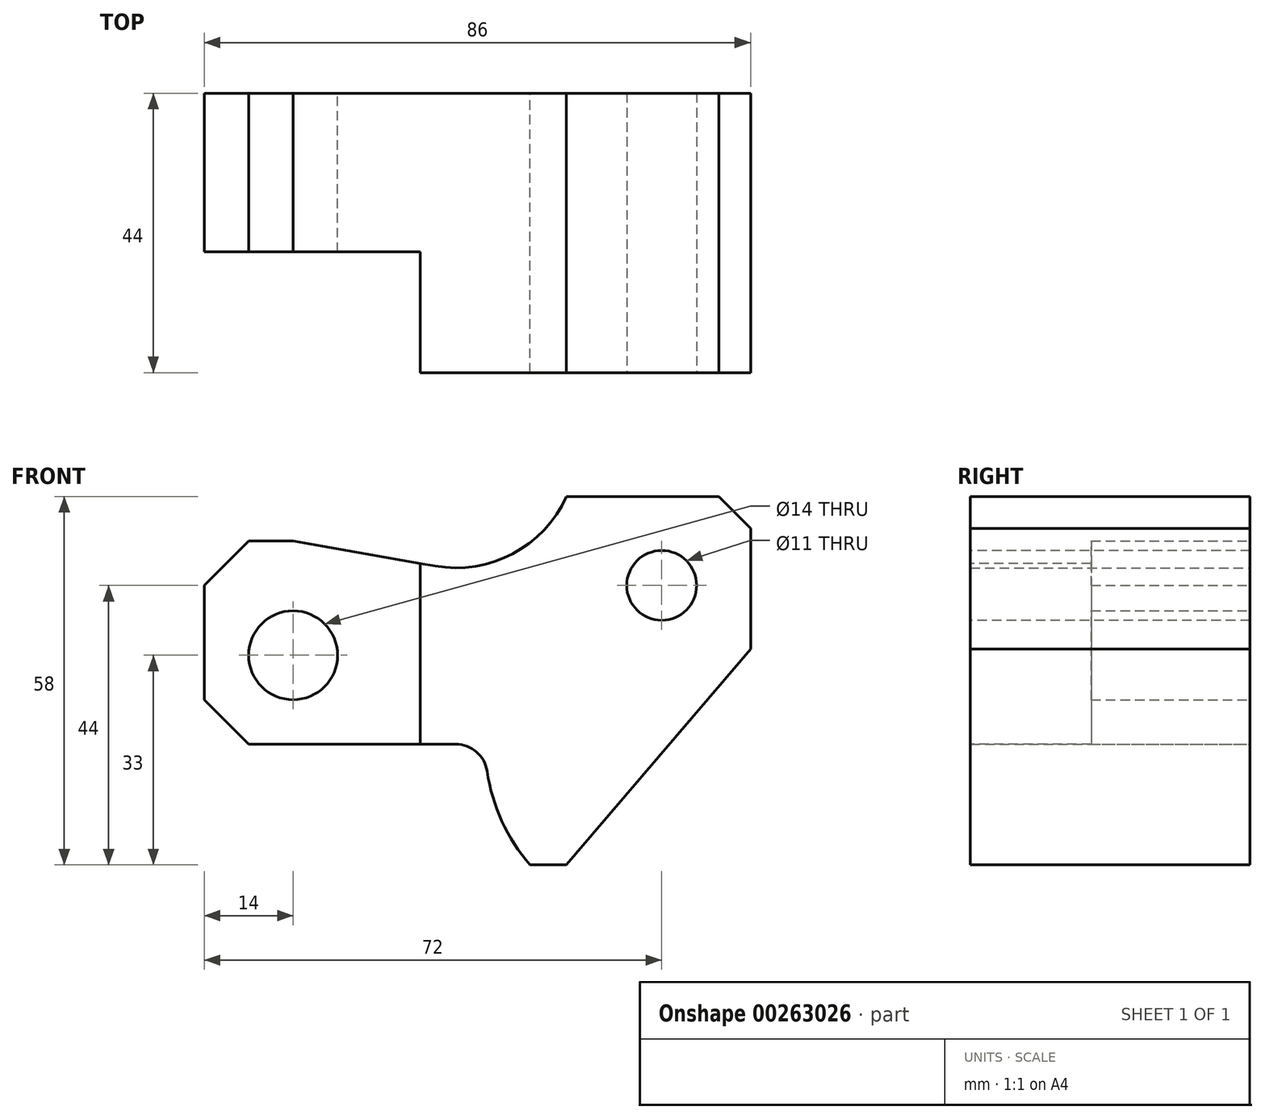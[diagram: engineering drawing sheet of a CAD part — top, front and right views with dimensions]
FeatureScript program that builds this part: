
annotation { "Feature Type Name" : "Feature", "Feature Type Description" : "" }
export const myFeature = defineFeature(function(context is Context, id is Id, definition is map)
    precondition{}
    {
        {
            var Q0;
            Q0=qCreatedBy(makeId("Front.planeOp"),FACE);
            var sketch = newSketch(context, id + "F0", { "sketchPlane" : qUnion([Q0])});
            skCircle(sketch, "E0", {"center": v(0, 0) * mm, "radius": 7 * mm});
            skLineSegment(sketch, "E1", {"start": v(-14, 11) * mm, "end": v(-14, -7) * mm});
            skLineSegment(sketch, "E2", {"start": v(-14, -7) * mm, "end": v(-7, -14) * mm});
            skLineSegment(sketch, "E3", {"start": v(-7, -14) * mm, "end": v(25.58, -14) * mm});
            skLineSegment(sketch, "E4", {"start": v(-14, 11) * mm, "end": v(-7, 18) * mm});
            skLineSegment(sketch, "E5", {"start": v(-7, 18) * mm, "end": v(0, 18) * mm});
            skLineSegment(sketch, "E6", {"start": v(0, 18) * mm, "end": v(22.36, 14.06) * mm});
            skArc(sketch, "E7", {"start": v(22.36, 14.06) * mm, "mid": v(34.56, 15.98) * mm, "end": v(43, 25) * mm});
            skArc(sketch, "E8", {"start": v(30.52, -18.26) * mm, "mid": v(28.84, -15.21) * mm, "end": v(25.58, -14) * mm});
            skArc(sketch, "E9", {"start": v(30.52, -18.26) * mm, "mid": v(32.86, -26.12) * mm, "end": v(37.3, -33) * mm});
            skLineSegment(sketch, "E10", {"start": v(37.3, -33) * mm, "end": v(43, -33) * mm});
            skLineSegment(sketch, "E11", {"start": v(43, -33) * mm, "end": v(72, 1) * mm});
            skLineSegment(sketch, "E12", {"start": v(72, 1) * mm, "end": v(72, 20) * mm});
            skLineSegment(sketch, "E13", {"start": v(72, 20) * mm, "end": v(67, 25) * mm});
            skLineSegment(sketch, "E14", {"start": v(67, 25) * mm, "end": v(43, 25) * mm});
            skSolve(sketch);
        }
        {
            var Q0;
            Q0=makeQuery(id+"F0.imprint","IMPRINT",FACE,{"disambiguationData":[TD([[makeQuery(id+"F0.imprint","IMPRINT",EDGE,{"derivedFrom":sQuery(id+"F0.wireOp",EDGE,"E0")}),-1.0]])]});
            extrude(context, id + "F1", {"entities" : qUnion([Q0]), "depth" : 44 * mm});
        }
        {
            var Q0;
            Q0=makeQuery(id+"F1.opExtrude","CAP_FACE",FACE,{"disambiguationData":[OSD([sQuery(id+"F0.wireOp",EDGE,"E0"),sQuery(id+"F0.wireOp",EDGE,"E1"),sQuery(id+"F0.wireOp",EDGE,"E2"),sQuery(id+"F0.wireOp",EDGE,"E3"),sQuery(id+"F0.wireOp",EDGE,"E4"),sQuery(id+"F0.wireOp",EDGE,"E5"),sQuery(id+"F0.wireOp",EDGE,"E6"),sQuery(id+"F0.wireOp",EDGE,"E7"),sQuery(id+"F0.wireOp",EDGE,"E8"),sQuery(id+"F0.wireOp",EDGE,"E9"),sQuery(id+"F0.wireOp",EDGE,"E10"),sQuery(id+"F0.wireOp",EDGE,"E11"),sQuery(id+"F0.wireOp",EDGE,"E12"),sQuery(id+"F0.wireOp",EDGE,"E13"),sQuery(id+"F0.wireOp",EDGE,"E14")])],"isStart":false});
            var sketch = newSketch(context, id + "F2", { "sketchPlane" : qUnion([Q0])});
            skCircle(sketch, "E15", {"center": v(58, 11) * mm, "radius": 5.5 * mm});
            skLineSegment(sketch, "E16", {"start": v(20, 14.47) * mm, "end": v(20, -14) * mm});
            skLineSegment(sketch, "E17", {"start": v(20, -14) * mm, "end": v(72, -14) * mm});
            skLineSegment(sketch, "E18", {"start": v(20, 14.47) * mm, "end": v(0, 18) * mm});
            skLineSegment(sketch, "E19", {"start": v(0, 18) * mm, "end": v(-7, 18) * mm});
            skLineSegment(sketch, "E20", {"start": v(-7, 18) * mm, "end": v(-14, 11) * mm});
            skLineSegment(sketch, "E21", {"start": v(-14, 11) * mm, "end": v(-14, -7) * mm});
            skLineSegment(sketch, "E22", {"start": v(-14, -7) * mm, "end": v(-7, -14) * mm});
            skLineSegment(sketch, "E23", {"start": v(-7, -14) * mm, "end": v(20, -14) * mm});
            skSolve(sketch);
        }
        {
            var Q0;
            Q0=makeQuery(id+"F2.imprint","IMPRINT",FACE,{"disambiguationData":[TD([[makeQuery(id+"F2.imprint","IMPRINT",EDGE,{"derivedFrom":sQuery(id+"F2.wireOp",EDGE,"E16")}),-1.0]])]});
            extrude(context, id + "F3", {"entities" : qUnion([Q0]), "operationType" : NewBodyOperationType.REMOVE, "oppositeDirection" : true, "depth" : 19 * mm});
        }
        {
            var Q0;
            Q0=makeQuery(id+"F2.imprint","IMPRINT",FACE,{"disambiguationData":[TD([[makeQuery(id+"F2.imprint","IMPRINT",EDGE,{"derivedFrom":sQuery(id+"F2.wireOp",EDGE,"E15")}),1.0]])]});
            extrude(context, id + "F4", {"entities" : qUnion([Q0]), "operationType" : NewBodyOperationType.REMOVE, "endBound" : BoundingType.THROUGH_ALL, "oppositeDirection" : true, "depth" : 25 * mm});
        }
    });
